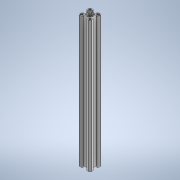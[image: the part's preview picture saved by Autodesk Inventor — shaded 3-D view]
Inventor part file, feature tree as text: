
AUTODESK INVENTOR PART (.ipt)
format: ipt  version: 2020 (Build 240168000, 168)  size: 6,814,208 bytes
history: native  units: in
note: dims shown in document units (in); Inventor stores cm internally (conversion verified against a paired STEP export)
features: extrude x1, sketch x1
ambient origin geometry x8: Origin, YZ Plane, XZ Plane, XY Plane, X Axis, Y Axis, Z Axis, Center Point
bodies: Solid1 (feature_tree)
feature tree (2):
  extrude  "Extrusion1"  Depth=3.875in TaperAngle=0.0deg
  sketch  "Sketch1"  dims[d0=0.5in d1=3.875in d2=0.0in]
